# Revit family: 13011-presto
name_source: partatom
category: Plumbing Fixtures
units: mm (PartAtom-declared; Revit-internal decimal feet)

## family parameters
Always vertical = Yes
Cut with Voids When Loaded = No
Maintain Annotation Orientation = No
OmniClass Number = 23.45.00.00
OmniClass Title = Sanitary, Laundry, and Cleaning Equipment
Part Type = Normal
Room Calculation Point = No
Round Connector Dimension = Use Diameter
Shared = No
Work Plane-Based = Yes

## types (1)
- 13011- Les Robinets PRESTO
    - Hydraulic supply = 15.00 mm
    > Standards & approvals = Brass body in accordance with EN 1982, EN 12164, EN 12165
Molded chrome-plated body in accordance with EN 12540
200-hour neutral salt spray resistant (NSS) in accordance with ISO 9227
    Default Elevation = 1219 mm
    Description = 13011 - PRESTO ECLAIR XL
    Model = 13011
    Recommended pressure = 3.0 Pa
    URL = https://www.prestodatashare.com
    brand = Les Robinets PRESTO
    flow = 0.1 L/s
    flow time = 9.0 s
    material = Chrome-plated brass body
    min pressure = 1.0 Pa
    pressure = 5.0 Pa
    range = Self-Closing flush valves
    ref = Ref: 13011 - PRESTO ECLAIR XL

## geometry (parser evidence)
native form markers: Sweep x2
no freeform markers — native parametric forms only
